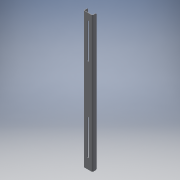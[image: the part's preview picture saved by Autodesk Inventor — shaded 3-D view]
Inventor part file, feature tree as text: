
AUTODESK INVENTOR PART (.ipt)
format: ipt  version: 2016 (Build 200138000, 138)  size: 162,304 bytes
history: native  units: mm
features: sheet_metal_op x2, sketch x2, chamfer x1, extrude x1, pattern_linear x1, other x1
ambient origin geometry x8: Origin, YZ Plane, XZ Plane, XY Plane, X Axis, Y Axis, Z Axis, Center Point
bodies: Solid1 (feature_tree)
feature tree (8):
  sheet_metal_op  "Contour Flange1"
  chamfer  "Corner Round1"
  extrude  "Extrusion1"  Depth=20.0mm
  pattern_linear  "Rectangular Pattern1"  Spacing1=3.0mm  [1 undecoded]
  sketch  "Sketch1"  dims[d0=20.0mm d1=20.0mm]
  other  "Plate1"
  sheet_metal_op  "Bend1"
  sketch  "Sketch2"  dims[d2=44.0mm d3=3.0mm d4=1.5mm d5=6.0mm d6=3.0mm d8=3.0mm d9=3.0mm d10=12.0mm d11=3.0mm d12=3.0mm d13=6.0mm d16=9.525mm d18=9.525mm d19=9.525mm d21=10.0mm d22=0.0mm d23=20.0mm d25=461.25mm]
note: 1 required parameter value undecoded (feature->parameter linkage not recoverable at this tier; creation-order binding heuristic only, values carry confidence <= 0.55)
